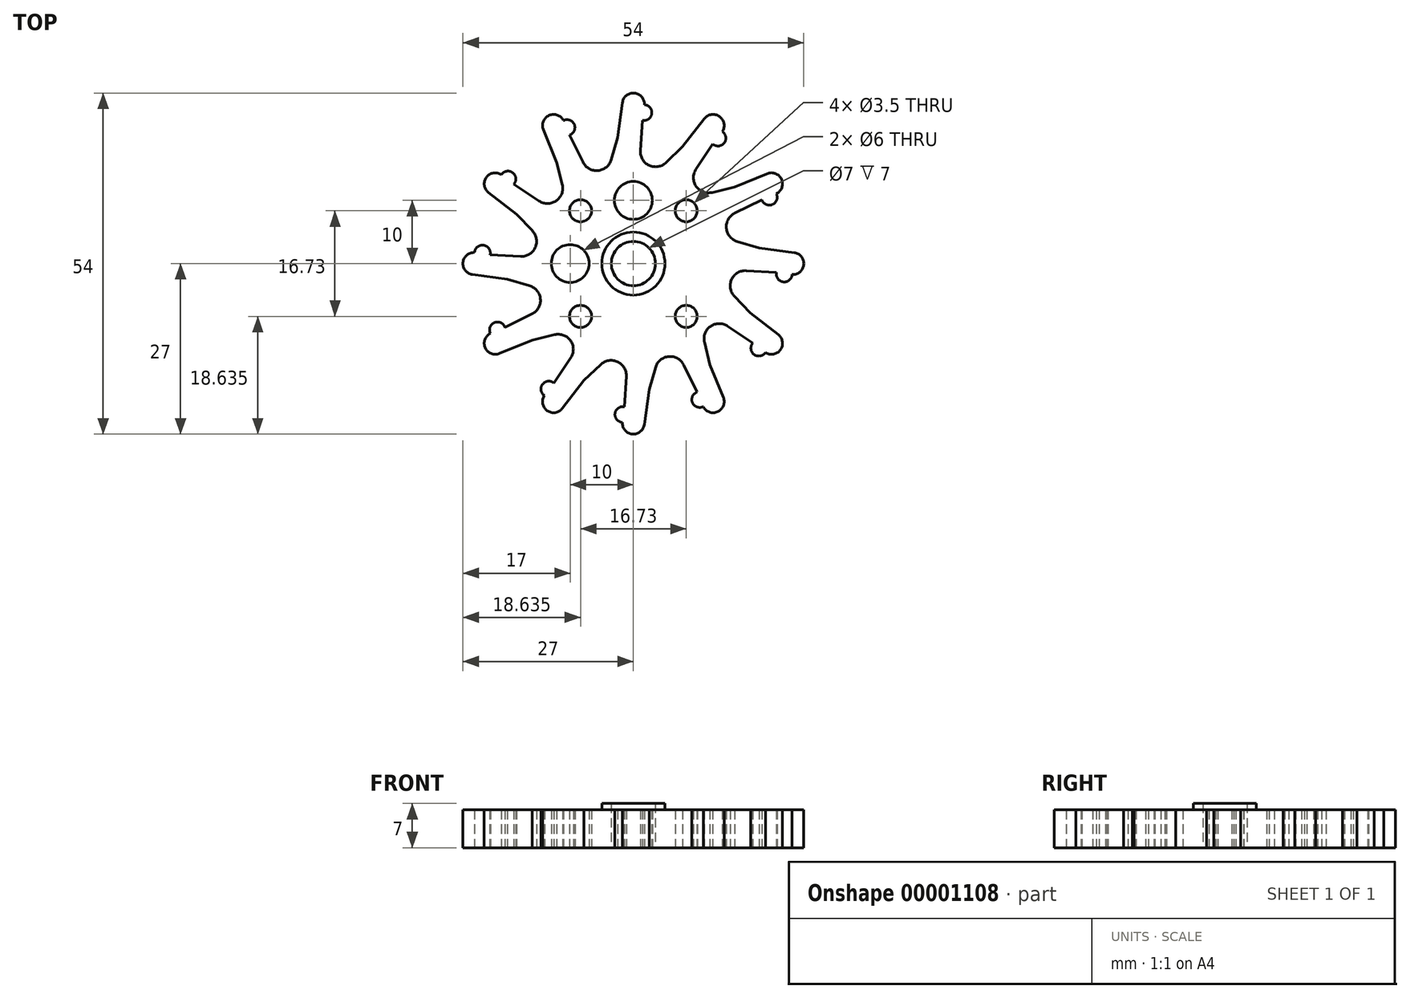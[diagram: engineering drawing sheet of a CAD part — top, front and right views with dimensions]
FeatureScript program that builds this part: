
annotation { "Feature Type Name" : "Feature", "Feature Type Description" : "" }
export const myFeature = defineFeature(function(context is Context, id is Id, definition is map)
    precondition{}
    {
        {
            var Q0;
            Q0=qCreatedBy(makeId("Top.planeOp"),FACE);
            var sketch = newSketch(context, id + "F0", { "sketchPlane" : qUnion([Q0])});
            skCircle(sketch, "E0", {"center": v(0, 0) * mm, "radius": 3.5 * mm});
            skLineSegment(sketch, "E1.0", {"start": v(9.95, 12.2) * mm, "end": v(14.72, 5.6) * mm, "construction": true});
            skLineSegment(sketch, "E1.1", {"start": v(14.72, 5.6) * mm, "end": v(15.55, -2.51) * mm, "construction": true});
            skLineSegment(sketch, "E1.2", {"start": v(15.55, -2.51) * mm, "end": v(12.2, -9.95) * mm, "construction": true});
            skLineSegment(sketch, "E1.3", {"start": v(12.2, -9.95) * mm, "end": v(5.6, -14.72) * mm, "construction": true});
            skLineSegment(sketch, "E1.4", {"start": v(5.6, -14.72) * mm, "end": v(-2.51, -15.55) * mm, "construction": true});
            skLineSegment(sketch, "E1.5", {"start": v(-2.51, -15.55) * mm, "end": v(-9.95, -12.2) * mm, "construction": true});
            skLineSegment(sketch, "E1.6", {"start": v(-9.95, -12.2) * mm, "end": v(-14.72, -5.6) * mm, "construction": true});
            skLineSegment(sketch, "E1.7", {"start": v(-14.72, -5.6) * mm, "end": v(-15.55, 2.51) * mm, "construction": true});
            skLineSegment(sketch, "E1.8", {"start": v(-15.55, 2.51) * mm, "end": v(-12.2, 9.95) * mm, "construction": true});
            skLineSegment(sketch, "E1.9", {"start": v(-12.2, 9.95) * mm, "end": v(-5.6, 14.72) * mm, "construction": true});
            skLineSegment(sketch, "E1.10", {"start": v(-5.6, 14.72) * mm, "end": v(2.51, 15.55) * mm, "construction": true});
            skLineSegment(sketch, "E1.11", {"start": v(2.51, 15.55) * mm, "end": v(9.95, 12.2) * mm, "construction": true});
            skLineSegment(sketch, "E2.0", {"start": v(7.81, 18.51) * mm, "end": v(16.02, 12.13) * mm, "construction": true});
            skLineSegment(sketch, "E2.1", {"start": v(16.02, 12.13) * mm, "end": v(19.94, 2.5) * mm, "construction": true});
            skLineSegment(sketch, "E2.2", {"start": v(19.94, 2.5) * mm, "end": v(18.51, -7.81) * mm, "construction": true});
            skLineSegment(sketch, "E2.3", {"start": v(18.51, -7.81) * mm, "end": v(12.13, -16.02) * mm, "construction": true});
            skLineSegment(sketch, "E2.4", {"start": v(12.13, -16.02) * mm, "end": v(2.5, -19.94) * mm, "construction": true});
            skLineSegment(sketch, "E2.5", {"start": v(2.5, -19.94) * mm, "end": v(-7.81, -18.51) * mm, "construction": true});
            skLineSegment(sketch, "E2.6", {"start": v(-7.81, -18.51) * mm, "end": v(-16.02, -12.13) * mm, "construction": true});
            skLineSegment(sketch, "E2.7", {"start": v(-16.02, -12.13) * mm, "end": v(-19.94, -2.5) * mm, "construction": true});
            skLineSegment(sketch, "E2.8", {"start": v(-19.94, -2.5) * mm, "end": v(-18.51, 7.81) * mm, "construction": true});
            skLineSegment(sketch, "E2.9", {"start": v(-18.51, 7.81) * mm, "end": v(-12.13, 16.02) * mm, "construction": true});
            skLineSegment(sketch, "E2.10", {"start": v(-12.13, 16.02) * mm, "end": v(-2.5, 19.94) * mm, "construction": true});
            skLineSegment(sketch, "E2.11", {"start": v(-2.5, 19.94) * mm, "end": v(7.81, 18.51) * mm, "construction": true});
            skLineSegment(sketch, "E3", {"start": v(-9.04, 25.25) * mm, "end": v(11.04, 25.25) * mm, "construction": true});
            skArc(sketch, "E4", {"start": v(1.75, 25.15) * mm, "mid": v(0.17, 27) * mm, "end": v(-1.73, 25.49) * mm});
            skLineSegment(sketch, "E5", {"start": v(-2.5, 19.94) * mm, "end": v(-1.73, 25.49) * mm});
            skLineSegment(sketch, "E6", {"start": v(7.81, 18.51) * mm, "end": v(5.18, 16) * mm});
            skArc(sketch, "E7", {"start": v(1.12, 17.88) * mm, "mid": v(2.5, 15.55) * mm, "end": v(5.18, 16) * mm});
            skPoint(sketch, "E7.second.point", {"position": v(1.12, 17.88) * mm});
            skPoint(sketch, "E7.third.point", {"position": v(5.18, 16) * mm});
            skLineSegment(sketch, "E8.trimOffspring", {"start": v(1.12, 17.88) * mm, "end": v(1.42, 22.67) * mm});
            skLineSegment(sketch, "E9", {"start": v(-3.31, 23.9) * mm, "end": v(7.83, 23.9) * mm, "construction": true});
            skArc(sketch, "E10", {"start": v(1.42, 22.67) * mm, "mid": v(2.9, 23.74) * mm, "end": v(1.75, 25.15) * mm});
            skLineSegment(sketch, "E11", {"start": v(-2.5, 19.94) * mm, "end": v(-3.57, 15.34) * mm});
            skLineSegment(sketch, "E12", {"start": v(6.94, 14.14) * mm, "end": v(7.81, 18.51) * mm});
            skArc(sketch, "E13", {"start": v(6.94, 14.14) * mm, "mid": v(5.31, 14.83) * mm, "end": v(3.62, 15.33) * mm});
            skArc(sketch, "E14.trimOffspring", {"start": v(2.51, 15.55) * mm, "mid": v(-0.54, 15.74) * mm, "end": v(-3.57, 15.34) * mm});
            skLineSegment(sketch, "E15", {"start": v(-3.57, 15.34) * mm, "end": v(-5.74, -5.36) * mm});
            skLineSegment(sketch, "E16", {"start": v(-5.74, -5.36) * mm, "end": v(2.43, -5.82) * mm});
            skLineSegment(sketch, "E17", {"start": v(2.43, -5.82) * mm, "end": v(6.94, 4.24) * mm});
            skLineSegment(sketch, "E18", {"start": v(6.94, 4.24) * mm, "end": v(6.94, 14.14) * mm});
            skSolve(sketch);
        }
        {
            var Q0;
            Q0=makeQuery(id+"F0.imprint","IMPRINT",FACE,{"disambiguationData":[TD([[makeQuery(id+"F0.imprint","IMPRINT",EDGE,{"derivedFrom":sQuery(id+"F0.wireOp",EDGE,"E4")}),1.0]])]});
            var Q1;
            {var subQ2=sQuery(id+"F0.wireOp",EDGE,"E6");Q1=makeQuery(id+"F0.imprint","IMPRINT",FACE,{"disambiguationData":[TD([[makeQuery(id+"F0.imprint","IMPRINT",EDGE,{"derivedFrom":subQ2}),1.0]])]});}
            var Q2;
            Q2=makeQuery(id+"F0.imprint","IMPRINT",FACE,{"disambiguationData":[TD([[makeQuery(id+"F0.imprint","IMPRINT",EDGE,{"derivedFrom":sQuery(id+"F0.wireOp",EDGE,"E0")}),-1.0]])]});
            extrude(context, id + "F1", {"entities" : qUnion([Q0, Q1, Q2]), "depth" : 6 * mm});
        }
        {
            var Q0;
            Q0=makeQuery(id+"F1.opExtrude","SWEPT_BODY",BODY,{"disambiguationData":[OSD([sQuery(id+"F0.wireOp",EDGE,"E0"),sQuery(id+"F0.wireOp",EDGE,"E4"),sQuery(id+"F0.wireOp",EDGE,"E5"),sQuery(id+"F0.wireOp",EDGE,"E6"),sQuery(id+"F0.wireOp",EDGE,"E7"),sQuery(id+"F0.wireOp",EDGE,"E8.trimOffspring"),sQuery(id+"F0.wireOp",EDGE,"E10"),sQuery(id+"F0.wireOp",EDGE,"E11"),sQuery(id+"F0.wireOp",EDGE,"E12"),sQuery(id+"F0.wireOp",EDGE,"E15"),sQuery(id+"F0.wireOp",EDGE,"E16"),sQuery(id+"F0.wireOp",EDGE,"E17"),sQuery(id+"F0.wireOp",EDGE,"E18")])]});
            var Q1;
            Q1=sQuery(id+"F0.wireOp",EDGE,"E0");
            circularPattern(context, id + "F2", {"entities" : qUnion([Q0]), "axis" : qUnion([Q1]), "angle" : 360 * degree, "instanceCount" : 12, "equalSpace" : true});
        }
        {
            var Q0;
            Q0=makeQuery(id+"F1.opExtrude","SWEPT_BODY",BODY,{"disambiguationData":[OSD([sQuery(id+"F0.wireOp",EDGE,"E0"),sQuery(id+"F0.wireOp",EDGE,"E4"),sQuery(id+"F0.wireOp",EDGE,"E5"),sQuery(id+"F0.wireOp",EDGE,"E6"),sQuery(id+"F0.wireOp",EDGE,"E7"),sQuery(id+"F0.wireOp",EDGE,"E8.trimOffspring"),sQuery(id+"F0.wireOp",EDGE,"E10"),sQuery(id+"F0.wireOp",EDGE,"E11"),sQuery(id+"F0.wireOp",EDGE,"E12"),sQuery(id+"F0.wireOp",EDGE,"E15"),sQuery(id+"F0.wireOp",EDGE,"E16"),sQuery(id+"F0.wireOp",EDGE,"E17"),sQuery(id+"F0.wireOp",EDGE,"E18")])]});
            var Q1;
            Q1=makeQuery(id+"F2.opPattern","COPY",BODY,{"derivedFrom":makeQuery(id+"F1.opExtrude","SWEPT_BODY",BODY,{"disambiguationData":[OSD([sQuery(id+"F0.wireOp",EDGE,"E0"),sQuery(id+"F0.wireOp",EDGE,"E4"),sQuery(id+"F0.wireOp",EDGE,"E5"),sQuery(id+"F0.wireOp",EDGE,"E6"),sQuery(id+"F0.wireOp",EDGE,"E7"),sQuery(id+"F0.wireOp",EDGE,"E8.trimOffspring"),sQuery(id+"F0.wireOp",EDGE,"E10"),sQuery(id+"F0.wireOp",EDGE,"E11"),sQuery(id+"F0.wireOp",EDGE,"E12"),sQuery(id+"F0.wireOp",EDGE,"E15"),sQuery(id+"F0.wireOp",EDGE,"E16"),sQuery(id+"F0.wireOp",EDGE,"E17"),sQuery(id+"F0.wireOp",EDGE,"E18")])]}),"instanceName":"1"});
            var Q2;
            Q2=makeQuery(id+"F2.opPattern","COPY",BODY,{"derivedFrom":makeQuery(id+"F1.opExtrude","SWEPT_BODY",BODY,{"disambiguationData":[OSD([sQuery(id+"F0.wireOp",EDGE,"E0"),sQuery(id+"F0.wireOp",EDGE,"E4"),sQuery(id+"F0.wireOp",EDGE,"E5"),sQuery(id+"F0.wireOp",EDGE,"E6"),sQuery(id+"F0.wireOp",EDGE,"E7"),sQuery(id+"F0.wireOp",EDGE,"E8.trimOffspring"),sQuery(id+"F0.wireOp",EDGE,"E10"),sQuery(id+"F0.wireOp",EDGE,"E11"),sQuery(id+"F0.wireOp",EDGE,"E12"),sQuery(id+"F0.wireOp",EDGE,"E15"),sQuery(id+"F0.wireOp",EDGE,"E16"),sQuery(id+"F0.wireOp",EDGE,"E17"),sQuery(id+"F0.wireOp",EDGE,"E18")])]}),"instanceName":"2"});
            var Q3;
            Q3=makeQuery(id+"F2.opPattern","COPY",BODY,{"derivedFrom":makeQuery(id+"F1.opExtrude","SWEPT_BODY",BODY,{"disambiguationData":[OSD([sQuery(id+"F0.wireOp",EDGE,"E0"),sQuery(id+"F0.wireOp",EDGE,"E4"),sQuery(id+"F0.wireOp",EDGE,"E5"),sQuery(id+"F0.wireOp",EDGE,"E6"),sQuery(id+"F0.wireOp",EDGE,"E7"),sQuery(id+"F0.wireOp",EDGE,"E8.trimOffspring"),sQuery(id+"F0.wireOp",EDGE,"E10"),sQuery(id+"F0.wireOp",EDGE,"E11"),sQuery(id+"F0.wireOp",EDGE,"E12"),sQuery(id+"F0.wireOp",EDGE,"E15"),sQuery(id+"F0.wireOp",EDGE,"E16"),sQuery(id+"F0.wireOp",EDGE,"E17"),sQuery(id+"F0.wireOp",EDGE,"E18")])]}),"instanceName":"3"});
            var Q4;
            Q4=makeQuery(id+"F2.opPattern","COPY",BODY,{"derivedFrom":makeQuery(id+"F1.opExtrude","SWEPT_BODY",BODY,{"disambiguationData":[OSD([sQuery(id+"F0.wireOp",EDGE,"E0"),sQuery(id+"F0.wireOp",EDGE,"E4"),sQuery(id+"F0.wireOp",EDGE,"E5"),sQuery(id+"F0.wireOp",EDGE,"E6"),sQuery(id+"F0.wireOp",EDGE,"E7"),sQuery(id+"F0.wireOp",EDGE,"E8.trimOffspring"),sQuery(id+"F0.wireOp",EDGE,"E10"),sQuery(id+"F0.wireOp",EDGE,"E11"),sQuery(id+"F0.wireOp",EDGE,"E12"),sQuery(id+"F0.wireOp",EDGE,"E15"),sQuery(id+"F0.wireOp",EDGE,"E16"),sQuery(id+"F0.wireOp",EDGE,"E17"),sQuery(id+"F0.wireOp",EDGE,"E18")])]}),"instanceName":"4"});
            var Q5;
            Q5=makeQuery(id+"F2.opPattern","COPY",BODY,{"derivedFrom":makeQuery(id+"F1.opExtrude","SWEPT_BODY",BODY,{"disambiguationData":[OSD([sQuery(id+"F0.wireOp",EDGE,"E0"),sQuery(id+"F0.wireOp",EDGE,"E4"),sQuery(id+"F0.wireOp",EDGE,"E5"),sQuery(id+"F0.wireOp",EDGE,"E6"),sQuery(id+"F0.wireOp",EDGE,"E7"),sQuery(id+"F0.wireOp",EDGE,"E8.trimOffspring"),sQuery(id+"F0.wireOp",EDGE,"E10"),sQuery(id+"F0.wireOp",EDGE,"E11"),sQuery(id+"F0.wireOp",EDGE,"E12"),sQuery(id+"F0.wireOp",EDGE,"E15"),sQuery(id+"F0.wireOp",EDGE,"E16"),sQuery(id+"F0.wireOp",EDGE,"E17"),sQuery(id+"F0.wireOp",EDGE,"E18")])]}),"instanceName":"5"});
            var Q6;
            Q6=makeQuery(id+"F2.opPattern","COPY",BODY,{"derivedFrom":makeQuery(id+"F1.opExtrude","SWEPT_BODY",BODY,{"disambiguationData":[OSD([sQuery(id+"F0.wireOp",EDGE,"E0"),sQuery(id+"F0.wireOp",EDGE,"E4"),sQuery(id+"F0.wireOp",EDGE,"E5"),sQuery(id+"F0.wireOp",EDGE,"E6"),sQuery(id+"F0.wireOp",EDGE,"E7"),sQuery(id+"F0.wireOp",EDGE,"E8.trimOffspring"),sQuery(id+"F0.wireOp",EDGE,"E10"),sQuery(id+"F0.wireOp",EDGE,"E11"),sQuery(id+"F0.wireOp",EDGE,"E12"),sQuery(id+"F0.wireOp",EDGE,"E15"),sQuery(id+"F0.wireOp",EDGE,"E16"),sQuery(id+"F0.wireOp",EDGE,"E17"),sQuery(id+"F0.wireOp",EDGE,"E18")])]}),"instanceName":"6"});
            var Q7;
            Q7=makeQuery(id+"F2.opPattern","COPY",BODY,{"derivedFrom":makeQuery(id+"F1.opExtrude","SWEPT_BODY",BODY,{"disambiguationData":[OSD([sQuery(id+"F0.wireOp",EDGE,"E0"),sQuery(id+"F0.wireOp",EDGE,"E4"),sQuery(id+"F0.wireOp",EDGE,"E5"),sQuery(id+"F0.wireOp",EDGE,"E6"),sQuery(id+"F0.wireOp",EDGE,"E7"),sQuery(id+"F0.wireOp",EDGE,"E8.trimOffspring"),sQuery(id+"F0.wireOp",EDGE,"E10"),sQuery(id+"F0.wireOp",EDGE,"E11"),sQuery(id+"F0.wireOp",EDGE,"E12"),sQuery(id+"F0.wireOp",EDGE,"E15"),sQuery(id+"F0.wireOp",EDGE,"E16"),sQuery(id+"F0.wireOp",EDGE,"E17"),sQuery(id+"F0.wireOp",EDGE,"E18")])]}),"instanceName":"7"});
            var Q8;
            Q8=makeQuery(id+"F2.opPattern","COPY",BODY,{"derivedFrom":makeQuery(id+"F1.opExtrude","SWEPT_BODY",BODY,{"disambiguationData":[OSD([sQuery(id+"F0.wireOp",EDGE,"E0"),sQuery(id+"F0.wireOp",EDGE,"E4"),sQuery(id+"F0.wireOp",EDGE,"E5"),sQuery(id+"F0.wireOp",EDGE,"E6"),sQuery(id+"F0.wireOp",EDGE,"E7"),sQuery(id+"F0.wireOp",EDGE,"E8.trimOffspring"),sQuery(id+"F0.wireOp",EDGE,"E10"),sQuery(id+"F0.wireOp",EDGE,"E11"),sQuery(id+"F0.wireOp",EDGE,"E12"),sQuery(id+"F0.wireOp",EDGE,"E15"),sQuery(id+"F0.wireOp",EDGE,"E16"),sQuery(id+"F0.wireOp",EDGE,"E17"),sQuery(id+"F0.wireOp",EDGE,"E18")])]}),"instanceName":"8"});
            var Q9;
            Q9=makeQuery(id+"F2.opPattern","COPY",BODY,{"derivedFrom":makeQuery(id+"F1.opExtrude","SWEPT_BODY",BODY,{"disambiguationData":[OSD([sQuery(id+"F0.wireOp",EDGE,"E0"),sQuery(id+"F0.wireOp",EDGE,"E4"),sQuery(id+"F0.wireOp",EDGE,"E5"),sQuery(id+"F0.wireOp",EDGE,"E6"),sQuery(id+"F0.wireOp",EDGE,"E7"),sQuery(id+"F0.wireOp",EDGE,"E8.trimOffspring"),sQuery(id+"F0.wireOp",EDGE,"E10"),sQuery(id+"F0.wireOp",EDGE,"E11"),sQuery(id+"F0.wireOp",EDGE,"E12"),sQuery(id+"F0.wireOp",EDGE,"E15"),sQuery(id+"F0.wireOp",EDGE,"E16"),sQuery(id+"F0.wireOp",EDGE,"E17"),sQuery(id+"F0.wireOp",EDGE,"E18")])]}),"instanceName":"9"});
            var Q10;
            Q10=makeQuery(id+"F2.opPattern","COPY",BODY,{"derivedFrom":makeQuery(id+"F1.opExtrude","SWEPT_BODY",BODY,{"disambiguationData":[OSD([sQuery(id+"F0.wireOp",EDGE,"E0"),sQuery(id+"F0.wireOp",EDGE,"E4"),sQuery(id+"F0.wireOp",EDGE,"E5"),sQuery(id+"F0.wireOp",EDGE,"E6"),sQuery(id+"F0.wireOp",EDGE,"E7"),sQuery(id+"F0.wireOp",EDGE,"E8.trimOffspring"),sQuery(id+"F0.wireOp",EDGE,"E10"),sQuery(id+"F0.wireOp",EDGE,"E11"),sQuery(id+"F0.wireOp",EDGE,"E12"),sQuery(id+"F0.wireOp",EDGE,"E15"),sQuery(id+"F0.wireOp",EDGE,"E16"),sQuery(id+"F0.wireOp",EDGE,"E17"),sQuery(id+"F0.wireOp",EDGE,"E18")])]}),"instanceName":"10"});
            var Q11;
            Q11=makeQuery(id+"F2.opPattern","COPY",BODY,{"derivedFrom":makeQuery(id+"F1.opExtrude","SWEPT_BODY",BODY,{"disambiguationData":[OSD([sQuery(id+"F0.wireOp",EDGE,"E0"),sQuery(id+"F0.wireOp",EDGE,"E4"),sQuery(id+"F0.wireOp",EDGE,"E5"),sQuery(id+"F0.wireOp",EDGE,"E6"),sQuery(id+"F0.wireOp",EDGE,"E7"),sQuery(id+"F0.wireOp",EDGE,"E8.trimOffspring"),sQuery(id+"F0.wireOp",EDGE,"E10"),sQuery(id+"F0.wireOp",EDGE,"E11"),sQuery(id+"F0.wireOp",EDGE,"E12"),sQuery(id+"F0.wireOp",EDGE,"E15"),sQuery(id+"F0.wireOp",EDGE,"E16"),sQuery(id+"F0.wireOp",EDGE,"E17"),sQuery(id+"F0.wireOp",EDGE,"E18")])]}),"instanceName":"11"});
            booleanBodies(context, id + "F3", {"operationType" : BooleanOperationType.UNION, "tools" : qUnion([Q0, Q1, Q2, Q3, Q4, Q5, Q6, Q7, Q8, Q9, Q10, Q11])});
        }
        {
            var Q0;
            Q0=makeQuery(id+"F0.imprint","IMPRINT",FACE,{"disambiguationData":[TD([[makeQuery(id+"F0.imprint","IMPRINT",EDGE,{"derivedFrom":sQuery(id+"F0.wireOp",EDGE,"E0")}),-1.0]])]});
            var sketch = newSketch(context, id + "F4", { "sketchPlane" : qUnion([Q0])});
            skCircle(sketch, "E19", {"center": v(0, 10) * mm, "radius": 3 * mm});
            skCircle(sketch, "E20.0.MirrorC", {"center": v(0, -10) * mm, "radius": 3 * mm});
            skCircle(sketch, "E21", {"center": v(-10, 0) * mm, "radius": 3 * mm});
            skCircle(sketch, "E22.0.MirrorC", {"center": v(10, 0) * mm, "radius": 3 * mm});
            skCircle(sketch, "E23", {"center": v(8.36, 8.36) * mm, "radius": 1.75 * mm});
            skCircle(sketch, "E24", {"center": v(-8.36, 8.36) * mm, "radius": 1.75 * mm});
            skCircle(sketch, "E25", {"center": v(-8.36, -8.36) * mm, "radius": 1.75 * mm});
            skCircle(sketch, "E26", {"center": v(8.36, -8.36) * mm, "radius": 1.75 * mm});
            skSolve(sketch);
        }
        {
            var Q0;
            {var subQ0=makeQuery(id+"F0.imprint","IMPRINT",EDGE,{"derivedFrom":sQuery(id+"F0.wireOp",EDGE,"E18")});var subQ1=sQuery(id+"F4.wireOp",EDGE,"E23");var subQ3=makeQuery(id+"F4.imprint","INTERSECT",VERTEX,{"disambiguationData":[OD(0.0)],"derivedFrom":[subQ0,subQ1]});Q0=qUnion([makeQuery(id+"F4.imprint","IMPRINT",FACE,{"disambiguationData":[TD([[makeQuery(id+"F4.imprint","IMPRINT",EDGE,{"derivedFrom":sQuery(id+"F4.wireOp",EDGE,"E20.0.MirrorC")}),-1.0]])]}),makeQuery(id+"F4.imprint","IMPRINT",FACE,{"disambiguationData":[TD([[makeQuery(id+"F4.imprint","IMPRINT",EDGE,{"derivedFrom":sQuery(id+"F4.wireOp",EDGE,"E21")}),1.0]])]}),makeQuery(id+"F4.imprint","IMPRINT",FACE,{"disambiguationData":[TD([[makeQuery(id+"F4.imprint","IMPRINT",EDGE,{"derivedFrom":sQuery(id+"F4.wireOp",EDGE,"E22.0.MirrorC")}),-1.0]])]}),makeQuery(id+"F4.imprint","IMPRINT",FACE,{"disambiguationData":[TD([[makeQuery(id+"F4.imprint","IMPRINT",EDGE,{"derivedFrom":sQuery(id+"F4.wireOp",EDGE,"E24")}),1.0]])]}),makeQuery(id+"F4.imprint","IMPRINT",FACE,{"disambiguationData":[TD([[makeQuery(id+"F4.imprint","IMPRINT",EDGE,{"derivedFrom":sQuery(id+"F4.wireOp",EDGE,"E25")}),1.0]])]}),makeQuery(id+"F4.imprint","IMPRINT",FACE,{"disambiguationData":[TD([[makeQuery(id+"F4.imprint","IMPRINT",EDGE,{"derivedFrom":sQuery(id+"F4.wireOp",EDGE,"E26")}),1.0]])]}),makeQuery(id+"F4.imprint","IMPRINT",FACE,{"disambiguationData":[TD([[makeQuery(id+"F4.imprint","IMPRINT",EDGE,{"derivedFrom":sQuery(id+"F4.wireOp",EDGE,"E19")}),1.0]])]}),makeQuery(id+"F4.imprint","IMPRINT",FACE,{"disambiguationData":[TD([[makeQuery(id+"F4.imprint","IMPRINT",EDGE,{"disambiguationData":[TD([[subQ3,1.0]])],"derivedFrom":subQ1}),1.0]])]}),makeQuery(id+"F4.imprint","IMPRINT",FACE,{"disambiguationData":[TD([[makeQuery(id+"F4.imprint","IMPRINT",EDGE,{"disambiguationData":[TD([[subQ3,-1.0]])],"derivedFrom":subQ1}),1.0]])]})]);}
            var Q1;
            {var subQ0=makeQuery(id+"F1.opExtrude","CAP_FACE",FACE,{"disambiguationData":[OSD([sQuery(id+"F0.wireOp",EDGE,"E0"),sQuery(id+"F0.wireOp",EDGE,"E4"),sQuery(id+"F0.wireOp",EDGE,"E5"),sQuery(id+"F0.wireOp",EDGE,"E6"),sQuery(id+"F0.wireOp",EDGE,"E7"),sQuery(id+"F0.wireOp",EDGE,"E8.trimOffspring"),sQuery(id+"F0.wireOp",EDGE,"E10"),sQuery(id+"F0.wireOp",EDGE,"E11"),sQuery(id+"F0.wireOp",EDGE,"E12"),sQuery(id+"F0.wireOp",EDGE,"E15"),sQuery(id+"F0.wireOp",EDGE,"E16"),sQuery(id+"F0.wireOp",EDGE,"E17"),sQuery(id+"F0.wireOp",EDGE,"E18")])],"isStart":true});Q1=makeQuery(id+"F3.opBoolean","MERGE",FACE,{"derivedFrom":[subQ0,makeQuery(id+"F2.opPattern","COPY",FACE,{"derivedFrom":subQ0,"instanceName":"1"}),makeQuery(id+"F2.opPattern","COPY",FACE,{"derivedFrom":subQ0,"instanceName":"2"}),makeQuery(id+"F2.opPattern","COPY",FACE,{"derivedFrom":subQ0,"instanceName":"3"}),makeQuery(id+"F2.opPattern","COPY",FACE,{"derivedFrom":subQ0,"instanceName":"4"}),makeQuery(id+"F2.opPattern","COPY",FACE,{"derivedFrom":subQ0,"instanceName":"5"}),makeQuery(id+"F2.opPattern","COPY",FACE,{"derivedFrom":subQ0,"instanceName":"6"}),makeQuery(id+"F2.opPattern","COPY",FACE,{"derivedFrom":subQ0,"instanceName":"7"}),makeQuery(id+"F2.opPattern","COPY",FACE,{"derivedFrom":subQ0,"instanceName":"8"}),makeQuery(id+"F2.opPattern","COPY",FACE,{"derivedFrom":subQ0,"instanceName":"9"}),makeQuery(id+"F2.opPattern","COPY",FACE,{"derivedFrom":subQ0,"instanceName":"10"}),makeQuery(id+"F2.opPattern","COPY",FACE,{"derivedFrom":subQ0,"instanceName":"11"})]});}
            extrude(context, id + "F5", {"entities" : qUnion([Q0]), "operationType" : NewBodyOperationType.REMOVE, "endBound" : BoundingType.THROUGH_ALL, "endBoundEntity" : qUnion([Q1]), "depth" : 25 * mm});
        }
        {
            var Q0;
            {var subQ0=makeQuery(id+"F1.opExtrude","CAP_FACE",FACE,{"disambiguationData":[OSD([sQuery(id+"F0.wireOp",EDGE,"E0"),sQuery(id+"F0.wireOp",EDGE,"E4"),sQuery(id+"F0.wireOp",EDGE,"E5"),sQuery(id+"F0.wireOp",EDGE,"E6"),sQuery(id+"F0.wireOp",EDGE,"E7"),sQuery(id+"F0.wireOp",EDGE,"E8.trimOffspring"),sQuery(id+"F0.wireOp",EDGE,"E10"),sQuery(id+"F0.wireOp",EDGE,"E11"),sQuery(id+"F0.wireOp",EDGE,"E12"),sQuery(id+"F0.wireOp",EDGE,"E15"),sQuery(id+"F0.wireOp",EDGE,"E16"),sQuery(id+"F0.wireOp",EDGE,"E17"),sQuery(id+"F0.wireOp",EDGE,"E18")])],"isStart":false});Q0=makeQuery(id+"F3.opBoolean","MERGE",FACE,{"derivedFrom":[subQ0,makeQuery(id+"F2.opPattern","COPY",FACE,{"derivedFrom":subQ0,"instanceName":"1"}),makeQuery(id+"F2.opPattern","COPY",FACE,{"derivedFrom":subQ0,"instanceName":"2"}),makeQuery(id+"F2.opPattern","COPY",FACE,{"derivedFrom":subQ0,"instanceName":"3"}),makeQuery(id+"F2.opPattern","COPY",FACE,{"derivedFrom":subQ0,"instanceName":"4"}),makeQuery(id+"F2.opPattern","COPY",FACE,{"derivedFrom":subQ0,"instanceName":"5"}),makeQuery(id+"F2.opPattern","COPY",FACE,{"derivedFrom":subQ0,"instanceName":"6"}),makeQuery(id+"F2.opPattern","COPY",FACE,{"derivedFrom":subQ0,"instanceName":"7"}),makeQuery(id+"F2.opPattern","COPY",FACE,{"derivedFrom":subQ0,"instanceName":"8"}),makeQuery(id+"F2.opPattern","COPY",FACE,{"derivedFrom":subQ0,"instanceName":"9"}),makeQuery(id+"F2.opPattern","COPY",FACE,{"derivedFrom":subQ0,"instanceName":"10"}),makeQuery(id+"F2.opPattern","COPY",FACE,{"derivedFrom":subQ0,"instanceName":"11"})]});}
            var sketch = newSketch(context, id + "F6", { "sketchPlane" : qUnion([Q0])});
            skCircle(sketch, "E27", {"center": v(0, 0) * mm, "radius": 5 * mm});
            skSolve(sketch);
        }
        {
            var Q0;
            Q0=makeQuery(id+"F6.imprint","IMPRINT",FACE,{"disambiguationData":[TD([[makeQuery(id+"F6.imprint","IMPRINT",EDGE,{"derivedFrom":sQuery(id+"F6.wireOp",EDGE,"E27")}),1.0]])]});
            extrude(context, id + "F7", {"entities" : qUnion([Q0]), "operationType" : NewBodyOperationType.ADD, "depth" : 1 * mm});
        }
    });
